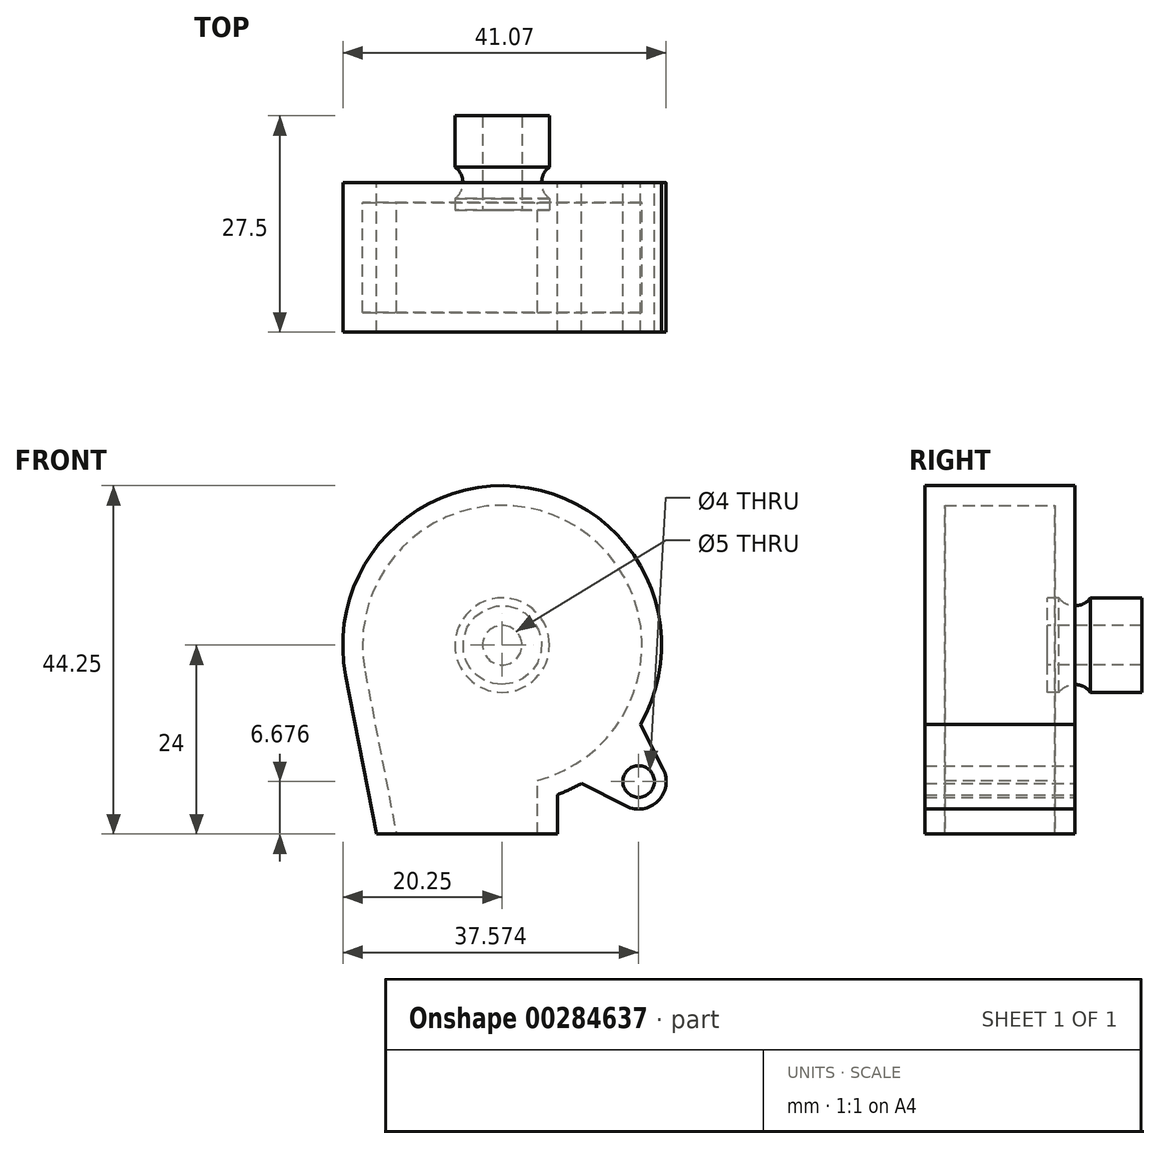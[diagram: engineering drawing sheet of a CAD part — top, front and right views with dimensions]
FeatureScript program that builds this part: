
annotation { "Feature Type Name" : "Feature", "Feature Type Description" : "" }
export const myFeature = defineFeature(function(context is Context, id is Id, definition is map)
    precondition{}
    {
        {
            var Q0;
            Q0=qCreatedBy(makeId("Top.planeOp"),FACE);
            var sketch = newSketch(context, id + "F0", { "sketchPlane" : qUnion([Q0])});
            skLineSegment(sketch, "E0.bottom", {"start": v(2.5, -3.5) * mm, "end": v(6, -3.5) * mm});
            skLineSegment(sketch, "E0.top", {"start": v(2.5, 8.5) * mm, "end": v(6, 8.5) * mm});
            skLineSegment(sketch, "E0.left", {"start": v(2.5, -3.5) * mm, "end": v(2.5, 8.5) * mm});
            skLineSegment(sketch, "E0.right", {"start": v(6, -3.5) * mm, "end": v(6, 8.5) * mm});
            skLineSegment(sketch, "E1", {"start": v(0, 0) * mm, "end": v(0, 18.49) * mm, "construction": true});
            skCircle(sketch, "E2", {"center": v(5.88, 0) * mm, "radius": 0.87 * mm, "construction": true});
            skCircle(sketch, "E3", {"center": v(7.5, 0) * mm, "radius": 2.5 * mm});
            skSolve(sketch);
        }
        {
            var Q0;
            {var subQ1=sQuery(id+"F0.wireOp",EDGE,"E0.bottom");Q0=makeQuery(id+"F0.imprint","IMPRINT",FACE,{"disambiguationData":[TD([[makeQuery(id+"F0.imprint","IMPRINT",EDGE,{"derivedFrom":subQ1}),1.0]])]});}
            var Q1;
            Q1=sQuery(id+"F0.wireOp",EDGE,"E1");
            revolve(context, id + "F1", {"entities" : qUnion([Q0]), "axis" : qUnion([Q1]), "revolveType" : RevolveType.FULL});
        }
        {
            var Q0;
            Q0=qCreatedBy(makeId("Top.planeOp"),FACE);
            var sketch = newSketch(context, id + "F2", { "sketchPlane" : qUnion([Q0])});
            skLineSegment(sketch, "E4", {"start": v(0, 0) * mm, "end": v(0, 0) * mm});
            skLineSegment(sketch, "E5", {"start": v(0, 0) * mm, "end": v(0, 20.84) * mm, "construction": true});
            skLineSegment(sketch, "E6.bottom", {"start": v(11.5, 0.7) * mm, "end": v(19, 0.7) * mm});
            skLineSegment(sketch, "E6.top", {"start": v(11.5, 19.3) * mm, "end": v(19, 19.3) * mm});
            skLineSegment(sketch, "E6.left", {"start": v(11.5, 0.7) * mm, "end": v(11.5, 19.3) * mm});
            skLineSegment(sketch, "E6.right", {"start": v(19, 0.7) * mm, "end": v(19, 19.3) * mm});
            skLineSegment(sketch, "E7.bottom", {"start": v(20.25, 0) * mm, "end": v(9, 0) * mm});
            skLineSegment(sketch, "E7.top", {"start": v(20.25, 20) * mm, "end": v(9, 20) * mm});
            skLineSegment(sketch, "E7.left", {"start": v(20.25, 0) * mm, "end": v(20.25, 20) * mm});
            skLineSegment(sketch, "E7.right", {"start": v(9, 0) * mm, "end": v(9, 20) * mm});
            skSolve(sketch);
        }
        {
            var Q0;
            Q0=qCreatedBy(makeId("Front.planeOp"),FACE);
            var sketch = newSketch(context, id + "F3", { "sketchPlane" : qUnion([Q0])});
            skCircle(sketch, "E8", {"center": v(0, 0) * mm, "radius": 20.25 * mm});
            skPoint(sketch, "E9.0", {"position": v(20.25, 0) * mm});
            skLineSegment(sketch, "E10", {"start": v(-19.88, -3.83) * mm, "end": v(-16, -24) * mm});
            skLineSegment(sketch, "E11", {"start": v(-16, -24) * mm, "end": v(7, -24) * mm});
            skLineSegment(sketch, "E12", {"start": v(7, -24) * mm, "end": v(7, -19) * mm});
            skLineSegment(sketch, "E13", {"start": v(0, 0) * mm, "end": v(17.32, -17.32) * mm, "construction": true});
            skCircle(sketch, "E14", {"center": v(17.32, -17.32) * mm, "radius": 2 * mm});
            skCircle(sketch, "E15", {"center": v(17.32, -17.32) * mm, "radius": 3.5 * mm});
            skLineSegment(sketch, "E16", {"start": v(20.44, -15.74) * mm, "end": v(17.56, -10.08) * mm});
            skLineSegment(sketch, "E17", {"start": v(15.74, -20.44) * mm, "end": v(10.08, -17.56) * mm});
            skSolve(sketch);
        }
        {
            var Q0;
            {var subQ0=sQuery(id+"F3.wireOp",EDGE,"E10");Q0=makeQuery(id+"F3.imprint","IMPRINT",FACE,{"disambiguationData":[TD([[makeQuery(id+"F3.imprint","IMPRINT",EDGE,{"derivedFrom":subQ0}),1.0]])]});}
            var Q1;
            {var subQ0=sQuery(id+"F3.wireOp",EDGE,"E8");var subQ1=makeQuery(id+"F3.imprint","INTERSECT",VERTEX,{"derivedFrom":[subQ0,sQuery(id+"F3.wireOp",EDGE,"E10")]});Q1=makeQuery(id+"F3.imprint","IMPRINT",FACE,{"disambiguationData":[TD([[makeQuery(id+"F3.imprint","IMPRINT",EDGE,{"disambiguationData":[TD([[subQ1,-1.0]])],"derivedFrom":subQ0}),1.0]])]});}
            extrude(context, id + "F4", {"entities" : qUnion([Q0, Q1]), "depth" : 19 * mm});
        }
        {
            var Q0;
            Q0=makeQuery(id+"F4.opExtrude","SWEPT_FACE",FACE,{"disambiguationData":[OSD([sQuery(id+"F3.wireOp",EDGE,"E11")])]});
            shell(context, id + "F5", {"entities" : qUnion([Q0]), "thickness" : 2.5 * mm});
        }
        {
            var Q0;
            {var subQ0=sQuery(id+"F3.wireOp",EDGE,"E16");Q0=makeQuery(id+"F3.imprint","IMPRINT",FACE,{"disambiguationData":[TD([[makeQuery(id+"F3.imprint","IMPRINT",EDGE,{"derivedFrom":subQ0}),1.0]])]});}
            var Q1;
            Q1=makeQuery(id+"F3.imprint","IMPRINT",FACE,{"disambiguationData":[TD([[makeQuery(id+"F3.imprint","IMPRINT",EDGE,{"derivedFrom":sQuery(id+"F3.wireOp",EDGE,"E14")}),-1.0]])]});
            var Q2;
            Q2=makeQuery(id+"F4.opExtrude","CAP_FACE",FACE,{"disambiguationData":[OSD([sQuery(id+"F3.wireOp",EDGE,"E8"),sQuery(id+"F3.wireOp",EDGE,"E10"),sQuery(id+"F3.wireOp",EDGE,"E11"),sQuery(id+"F3.wireOp",EDGE,"E12")])],"isStart":false});
            extrude(context, id + "F6", {"entities" : qUnion([Q0, Q1]), "operationType" : NewBodyOperationType.ADD, "endBound" : BoundingType.UP_TO_SURFACE, "endBoundEntityFace" : qUnion([Q2]), "depth" : 20 * mm});
        }
    });
